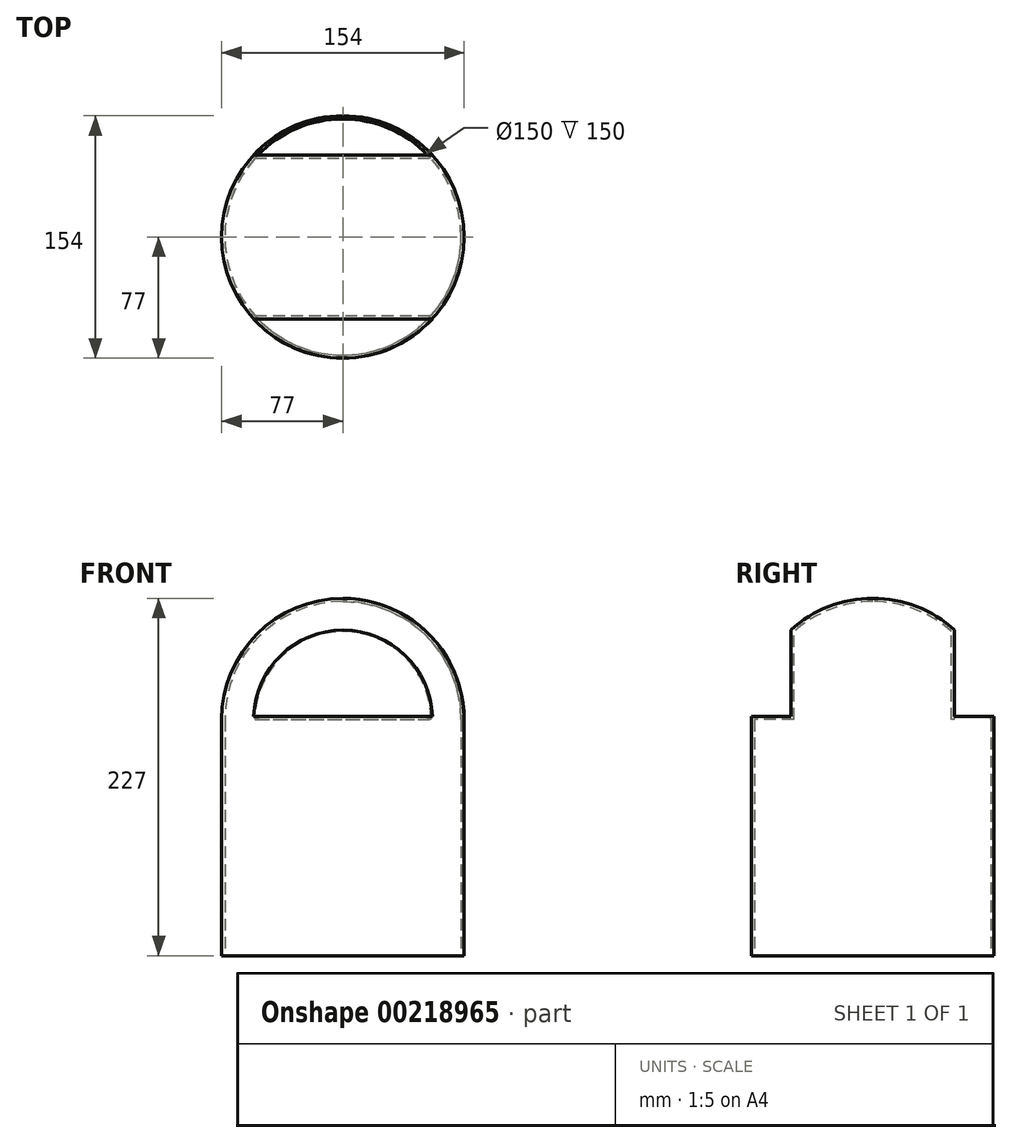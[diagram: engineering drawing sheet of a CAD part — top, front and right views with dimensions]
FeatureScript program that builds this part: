
annotation { "Feature Type Name" : "Feature", "Feature Type Description" : "" }
export const myFeature = defineFeature(function(context is Context, id is Id, definition is map)
    precondition{}
    {
        {
            assignVariable(context, id + "F0", {"name" : "wall", "anyValue" : 2});
        }
        {
            assignVariable(context, id + "F1", {"name" : "box", "anyValue" : 150});
        }
        {
            var Q0;
            Q0=qCreatedBy(makeId("Top.planeOp"),FACE);
            var sketch = newSketch(context, id + "F2", { "sketchPlane" : qUnion([Q0])});
            skLineSegment(sketch, "E0.bottom", {"start": v(-175, 125) * mm, "end": v(175, 125) * mm, "construction": true});
            skLineSegment(sketch, "E0.top", {"start": v(-175, -125) * mm, "end": v(175, -125) * mm, "construction": true});
            skLineSegment(sketch, "E0.left", {"start": v(-175, 125) * mm, "end": v(-175, -125) * mm, "construction": true});
            skLineSegment(sketch, "E0.right", {"start": v(175, 125) * mm, "end": v(175, -125) * mm, "construction": true});
            skCircle(sketch, "E1", {"center": v(0, 0) * mm, "radius": 75 * mm});
            skCircle(sketch, "E2.0", {"center": v(0, 0) * mm, "radius": 77 * mm});
            skLineSegment(sketch, "E3.bottom", {"start": v(-110, 110) * mm, "end": v(110, 110) * mm});
            skLineSegment(sketch, "E3.top", {"start": v(-110, -110) * mm, "end": v(110, -110) * mm});
            skLineSegment(sketch, "E3.left", {"start": v(-110, 110) * mm, "end": v(-110, -110) * mm});
            skLineSegment(sketch, "E3.right", {"start": v(110, 110) * mm, "end": v(110, -110) * mm});
            skLineSegment(sketch, "E4", {"start": v(0, 0) * mm, "end": v(-110, 0) * mm, "construction": true});
            skLineSegment(sketch, "E5", {"start": v(0, 0) * mm, "end": v(0, 110) * mm, "construction": true});
            skLineSegment(sketch, "E6", {"start": v(-55.9, -50) * mm, "end": v(55.9, -50) * mm});
            skLineSegment(sketch, "E7.MirrorCS", {"start": v(-55.9, 50) * mm, "end": v(55.9, 50) * mm});
            skSolve(sketch);
        }
        {
            var Q0;
            Q0=qCreatedBy(makeId("Top.planeOp"),FACE);
            cPlane(context, id + "F3", {"entities" : qUnion([Q0]), "cplaneType" : CPlaneType.OFFSET, "offset" : (getVariable(context, 'box')) * mm, "width" : 150 * mm, "height" : 150 * mm});
        }
        {
            var Q0;
            Q0=qCreatedBy(makeId("Top.planeOp"),FACE);
            cPlane(context, id + "F4", {"entities" : qUnion([Q0]), "cplaneType" : CPlaneType.OFFSET, "offset" : (getVariable(context, 'box') + getVariable(context, 'wall')) * mm, "width" : 150 * mm, "height" : 150 * mm});
        }
        {
            var Q0;
            Q0=qCreatedBy(id+"F3.planeOp",FACE);
            var sketch = newSketch(context, id + "F5", { "sketchPlane" : qUnion([Q0])});
            skCircle(sketch, "E8.0", {"center": v(0, 0) * mm, "radius": 75 * mm});
            skCircle(sketch, "E9.0", {"center": v(0, 0) * mm, "radius": 77 * mm});
            skLineSegment(sketch, "E10.0", {"start": v(-55.9, 50) * mm, "end": v(55.9, 50) * mm});
            skLineSegment(sketch, "E11.0", {"start": v(-55.9, -50) * mm, "end": v(55.9, -50) * mm});
            skLineSegment(sketch, "E12.0", {"start": v(-55.9, -52) * mm, "end": v(55.9, -52) * mm});
            skLineSegment(sketch, "E13.MirrorCS", {"start": v(-55.9, 52) * mm, "end": v(55.9, 52) * mm});
            skSolve(sketch);
        }
        {
            var Q0;
            Q0=qCreatedBy(id+"F4.planeOp",FACE);
            var sketch = newSketch(context, id + "F6", { "sketchPlane" : qUnion([Q0])});
            skCircle(sketch, "E14.0", {"center": v(0, 0) * mm, "radius": 77 * mm});
            skCircle(sketch, "E14.1", {"center": v(0, 0) * mm, "radius": 75 * mm});
            skLineSegment(sketch, "E14.2", {"start": v(-55.9, -52) * mm, "end": v(55.9, -52) * mm});
            skLineSegment(sketch, "E14.3", {"start": v(-55.9, 52) * mm, "end": v(55.9, 52) * mm});
            skLineSegment(sketch, "E15", {"start": v(55.9, -52) * mm, "end": v(56.79, -52) * mm});
            skLineSegment(sketch, "E16", {"start": v(-55.9, -52) * mm, "end": v(-56.79, -52) * mm});
            skLineSegment(sketch, "E17.MirrorCS", {"start": v(55.9, 52) * mm, "end": v(56.79, 52) * mm});
            skLineSegment(sketch, "E18.MirrorCS", {"start": v(-55.9, 52) * mm, "end": v(-56.79, 52) * mm});
            skSolve(sketch);
        }
        {
            var Q0;
            Q0=makeQuery(id+"F2.imprint","IMPRINT",FACE,{"disambiguationData":[TD([[makeQuery(id+"F2.imprint","IMPRINT",EDGE,{"derivedFrom":sQuery(id+"F2.wireOp",EDGE,"E1")}),-1.0]])]});
            extrude(context, id + "F7", {"entities" : qUnion([Q0]), "depth" : (getVariable(context, 'box')) * mm});
        }
        {
            var Q0;
            Q0=qCreatedBy(makeId("Front.planeOp"),FACE);
            var sketch = newSketch(context, id + "F8", { "sketchPlane" : qUnion([Q0])});
            skCircle(sketch, "E19", {"center": v(0, 150) * mm, "radius": 75 * mm});
            skCircle(sketch, "E20.0", {"center": v(0, 150) * mm, "radius": 77 * mm});
            skLineSegment(sketch, "E21.0", {"start": v(-77, 150) * mm, "end": v(77, 150) * mm});
            skLineSegment(sketch, "E22", {"start": v(0, 225) * mm, "end": v(0, 227) * mm});
            skCircle(sketch, "E23", {"center": v(0, 185) * mm, "radius": 4.75 * mm});
            skLineSegment(sketch, "E24", {"start": v(0, 185) * mm, "end": v(0, 177.1) * mm, "construction": true});
            skLineSegment(sketch, "E25", {"start": v(-17.5, 177.1) * mm, "end": v(17.5, 177.1) * mm, "construction": true});
            skPoint(sketch, "E26", {"position": v(0, 177.1) * mm});
            skCircle(sketch, "E27", {"center": v(-17.5, 177.1) * mm, "radius": 2.1 * mm});
            skCircle(sketch, "E28.MirrorC", {"center": v(17.5, 177.1) * mm, "radius": 2.1 * mm});
            skLineSegment(sketch, "E29", {"start": v(0, 150) * mm, "end": v(0, 225) * mm, "construction": true});
            skSolve(sketch);
        }
        {
            var Q0;
            {var subQ0=sQuery(id+"F8.wireOp",EDGE,"E22");Q0=makeQuery(id+"F8.imprint","IMPRINT",FACE,{"disambiguationData":[TD([[makeQuery(id+"F8.imprint","IMPRINT",EDGE,{"derivedFrom":subQ0}),1.0]])]});}
            var Q1;
            Q1=sQuery(id+"F8.wireOp",EDGE,"E22");
            revolve(context, id + "F9", {"entities" : qUnion([Q0]), "axis" : qUnion([Q1]), "revolveType" : RevolveType.FULL});
        }
        {
            var Q0;
            Q0=makeQuery(id+"F8.imprint","IMPRINT",FACE,{"disambiguationData":[TD([[makeQuery(id+"F8.imprint","IMPRINT",EDGE,{"derivedFrom":sQuery(id+"F8.wireOp",EDGE,"E23")}),1.0]])]});
            extrude(context, id + "F10", {"entities" : qUnion([Q0]), "operationType" : NewBodyOperationType.REMOVE, "depth" : 120 * mm, "hasSecondDirection" : true, "secondDirectionOppositeDirection" : true, "secondDirectionDepth" : 120 * mm});
        }
        {
            var Q0;
            {var subQ0=sQuery(id+"F5.wireOp",EDGE,"E11.0");Q0=makeQuery(id+"F5.imprint","IMPRINT",FACE,{"disambiguationData":[TD([[makeQuery(id+"F5.imprint","IMPRINT",EDGE,{"derivedFrom":subQ0}),-1.0]])]});}
            var Q1;
            {var subQ0=sQuery(id+"F5.wireOp",EDGE,"E10.0");Q1=makeQuery(id+"F5.imprint","IMPRINT",FACE,{"disambiguationData":[TD([[makeQuery(id+"F5.imprint","IMPRINT",EDGE,{"derivedFrom":subQ0}),1.0]])]});}
            var Q2;
            Q2=makeQuery(id+"F9.opRevolve","SWEPT_FACE",FACE,{"disambiguationData":[OSD([sQuery(id+"F8.wireOp",EDGE,"E20.0")])]});
            extrude(context, id + "F11", {"entities" : qUnion([Q0, Q1]), "operationType" : NewBodyOperationType.ADD, "endBound" : BoundingType.UP_TO_SURFACE, "endBoundEntityFace" : qUnion([Q2]), "depth" : 25 * mm});
        }
        {
            var Q0;
            {var subQ0=sQuery(id+"F5.wireOp",EDGE,"E13.MirrorCS");var subQ1=sQuery(id+"F5.wireOp",EDGE,"E8.0");var subQ2=makeQuery(id+"F5.imprint","INTERSECT",VERTEX,{"disambiguationData":[OD(0.0)],"derivedFrom":[subQ1,subQ0]});Q0=makeQuery(id+"F5.imprint","IMPRINT",FACE,{"disambiguationData":[TD([[makeQuery(id+"F5.imprint","IMPRINT",EDGE,{"disambiguationData":[TD([[subQ2,-1.0]])],"derivedFrom":subQ1}),1.0]])]});}
            var Q1;
            {var subQ0=sQuery(id+"F5.wireOp",EDGE,"E12.0");var subQ1=sQuery(id+"F5.wireOp",EDGE,"E8.0");var subQ2=makeQuery(id+"F5.imprint","INTERSECT",VERTEX,{"disambiguationData":[OD(0.0)],"derivedFrom":[subQ1,subQ0]});Q1=makeQuery(id+"F5.imprint","IMPRINT",FACE,{"disambiguationData":[TD([[makeQuery(id+"F5.imprint","IMPRINT",EDGE,{"disambiguationData":[TD([[subQ2,-1.0]])],"derivedFrom":subQ1}),1.0]])]});}
            extrude(context, id + "F12", {"entities" : qUnion([Q0, Q1]), "operationType" : NewBodyOperationType.ADD, "depth" : (getVariable(context, 'wall')) * mm});
        }
        {
            var Q0;
            {var subQ0=sQuery(id+"F6.wireOp",EDGE,"E14.2");var subQ1=sQuery(id+"F6.wireOp",EDGE,"E14.1");var subQ2=makeQuery(id+"F6.imprint","INTERSECT",VERTEX,{"disambiguationData":[OD(0.0)],"derivedFrom":[subQ1,subQ0]});Q0=makeQuery(id+"F6.imprint","IMPRINT",FACE,{"disambiguationData":[TD([[makeQuery(id+"F6.imprint","IMPRINT",EDGE,{"disambiguationData":[TD([[subQ2,-1.0]])],"derivedFrom":subQ1}),1.0]])]});}
            var Q1;
            {var subQ0=sQuery(id+"F6.wireOp",EDGE,"E15");Q1=makeQuery(id+"F6.imprint","IMPRINT",FACE,{"disambiguationData":[TD([[makeQuery(id+"F6.imprint","IMPRINT",EDGE,{"derivedFrom":subQ0}),-1.0]])]});}
            var Q2;
            {var subQ0=sQuery(id+"F6.wireOp",EDGE,"E14.3");var subQ1=sQuery(id+"F6.wireOp",EDGE,"E14.1");var subQ2=makeQuery(id+"F6.imprint","INTERSECT",VERTEX,{"disambiguationData":[OD(0.0)],"derivedFrom":[subQ1,subQ0]});Q2=makeQuery(id+"F6.imprint","IMPRINT",FACE,{"disambiguationData":[TD([[makeQuery(id+"F6.imprint","IMPRINT",EDGE,{"disambiguationData":[TD([[subQ2,1.0]])],"derivedFrom":subQ1}),1.0]])]});}
            var Q3;
            {var subQ0=sQuery(id+"F6.wireOp",EDGE,"E17.MirrorCS");Q3=makeQuery(id+"F6.imprint","IMPRINT",FACE,{"disambiguationData":[TD([[makeQuery(id+"F6.imprint","IMPRINT",EDGE,{"derivedFrom":subQ0}),1.0]])]});}
            extrude(context, id + "F13", {"entities" : qUnion([Q0, Q1, Q2, Q3]), "operationType" : NewBodyOperationType.REMOVE, "endBound" : BoundingType.THROUGH_ALL, "depth" : 25 * mm});
        }
    });
